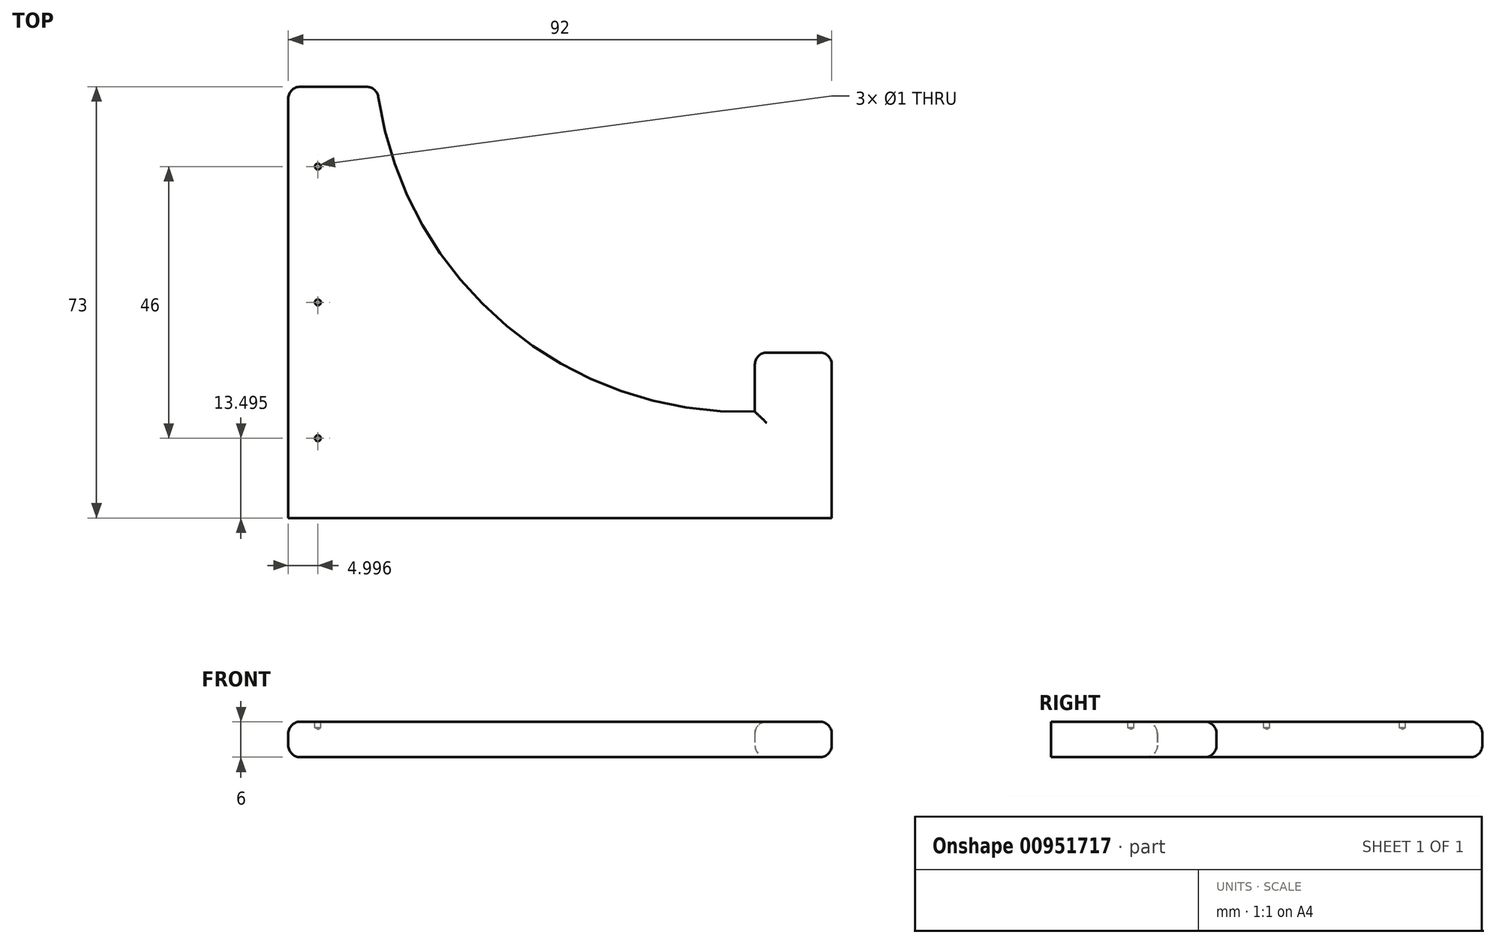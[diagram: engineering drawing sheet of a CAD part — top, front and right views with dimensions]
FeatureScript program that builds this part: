
annotation { "Feature Type Name" : "Feature", "Feature Type Description" : "" }
export const myFeature = defineFeature(function(context is Context, id is Id, definition is map)
    precondition{}
    {
        {
            var Q0;
            Q0=qCreatedBy(makeId("Top.planeOp"),FACE);
            var sketch = newSketch(context, id + "F0", { "sketchPlane" : qUnion([Q0])});
            skLineSegment(sketch, "E0.bottom", {"start": v(-43.17, -8.37) * mm, "end": v(48.83, -8.37) * mm});
            skLineSegment(sketch, "E0.top", {"start": v(-43.17, 64.63) * mm, "end": v(-28.17, 64.63) * mm});
            skLineSegment(sketch, "E0.left", {"start": v(-43.17, -8.37) * mm, "end": v(-43.17, 64.63) * mm});
            skLineSegment(sketch, "E0.right", {"start": v(48.83, -8.37) * mm, "end": v(48.83, 19.63) * mm});
            skLineSegment(sketch, "E1", {"start": v(35.83, 19.63) * mm, "end": v(48.83, 19.63) * mm});
            skLineSegment(sketch, "E2", {"start": v(35.83, 19.63) * mm, "end": v(35.83, 9.63) * mm});
            skArc(sketch, "E3", {"start": v(-28.17, 64.63) * mm, "mid": v(-6.85, 24.7) * mm, "end": v(35.83, 9.63) * mm});
            skSolve(sketch);
        }
        {
            var Q0;
            Q0=makeQuery(id+"F0.imprint","IMPRINT",FACE,{"disambiguationData":[TD([[makeQuery(id+"F0.imprint","IMPRINT",EDGE,{"derivedFrom":sQuery(id+"F0.wireOp",EDGE,"E0.bottom")}),1.0]])]});
            extrude(context, id + "F1", {"entities" : qUnion([Q0]), "depth" : 6 * mm, "offsetDistance" : 25 * mm});
        }
        {
            var Q0;
            Q0=makeQuery(id+"F1.opExtrude","CAP_FACE",FACE,{"disambiguationData":[OSD([sQuery(id+"F0.wireOp",EDGE,"E0.bottom"),sQuery(id+"F0.wireOp",EDGE,"E0.top"),sQuery(id+"F0.wireOp",EDGE,"E0.left"),sQuery(id+"F0.wireOp",EDGE,"E0.right"),sQuery(id+"F0.wireOp",EDGE,"E1"),sQuery(id+"F0.wireOp",EDGE,"E2"),sQuery(id+"F0.wireOp",EDGE,"E3")])],"isStart":false});
            var sketch = newSketch(context, id + "F2", { "sketchPlane" : qUnion([Q0])});
            skPoint(sketch, "E4", {"position": v(-38.17, 51.13) * mm});
            skPoint(sketch, "E5", {"position": v(-38.17, 28.13) * mm});
            skPoint(sketch, "E6", {"position": v(-38.17, 5.13) * mm});
            skSolve(sketch);
        }
        {
            var Q0;
            Q0=sQuery(id+"F2.wireOp",VERTEX,"E4");
            var Q1;
            Q1=sQuery(id+"F2.wireOp",VERTEX,"E5");
            var Q2;
            Q2=sQuery(id+"F2.wireOp",VERTEX,"E6");
            var Q3;
            Q3=makeQuery(id+"F1.opExtrude","SWEPT_BODY",BODY,{"disambiguationData":[OSD([sQuery(id+"F0.wireOp",EDGE,"E0.bottom"),sQuery(id+"F0.wireOp",EDGE,"E0.top"),sQuery(id+"F0.wireOp",EDGE,"E0.left"),sQuery(id+"F0.wireOp",EDGE,"E0.right"),sQuery(id+"F0.wireOp",EDGE,"E1"),sQuery(id+"F0.wireOp",EDGE,"E2"),sQuery(id+"F0.wireOp",EDGE,"E3")])]});
            hole(context, id + "F3", {"style" : HoleStyle.SIMPLE, "endStyle" : HoleEndStyle.BLIND, "holeDiameter" : 1 * mm, "majorDiameter" : 5 * mm, "holeDepth" : 1 * mm, "isTappedThrough" : true, "tappedDepth" : 12 * mm, "tapClearance" : 3, "locations" : qUnion([Q0, Q1, Q2]), "scope" : qUnion([Q3])});
        }
        {
            var Q0;
            Q0=makeQuery(id+"F1.opExtrude","SWEPT_EDGE",EDGE,{"disambiguationData":[OSD([sQuery(id+"F0.wireOp",EDGE,"E0.right"),sQuery(id+"F0.wireOp",EDGE,"E1")])]});
            var Q1;
            Q1=makeQuery(id+"F1.opExtrude","CAP_EDGE",EDGE,{"disambiguationData":[OSD([sQuery(id+"F0.wireOp",EDGE,"E0.right")])],"isStart":true});
            var Q2;
            Q2=makeQuery(id+"F1.opExtrude","CAP_EDGE",EDGE,{"disambiguationData":[OSD([sQuery(id+"F0.wireOp",EDGE,"E0.right")])],"isStart":false});
            var Q3;
            Q3=makeQuery(id+"F1.opExtrude","CAP_EDGE",EDGE,{"disambiguationData":[OSD([sQuery(id+"F0.wireOp",EDGE,"E1")])],"isStart":false});
            var Q4;
            Q4=makeQuery(id+"F1.opExtrude","CAP_EDGE",EDGE,{"disambiguationData":[OSD([sQuery(id+"F0.wireOp",EDGE,"E1")])],"isStart":true});
            var Q5;
            Q5=makeQuery(id+"F1.opExtrude","CAP_EDGE",EDGE,{"disambiguationData":[OSD([sQuery(id+"F0.wireOp",EDGE,"E2")])],"isStart":false});
            var Q6;
            Q6=makeQuery(id+"F1.opExtrude","CAP_EDGE",EDGE,{"disambiguationData":[OSD([sQuery(id+"F0.wireOp",EDGE,"E3")])],"isStart":false});
            var Q7;
            Q7=makeQuery(id+"F1.opExtrude","CAP_EDGE",EDGE,{"disambiguationData":[OSD([sQuery(id+"F0.wireOp",EDGE,"E2")])],"isStart":true});
            var Q8;
            Q8=makeQuery(id+"F1.opExtrude","CAP_EDGE",EDGE,{"disambiguationData":[OSD([sQuery(id+"F0.wireOp",EDGE,"E3")])],"isStart":true});
            var Q9;
            Q9=makeQuery(id+"F1.opExtrude","CAP_EDGE",EDGE,{"disambiguationData":[OSD([sQuery(id+"F0.wireOp",EDGE,"E0.top")])],"isStart":true});
            var Q10;
            Q10=makeQuery(id+"F1.opExtrude","CAP_EDGE",EDGE,{"disambiguationData":[OSD([sQuery(id+"F0.wireOp",EDGE,"E0.top")])],"isStart":false});
            var Q11;
            Q11=makeQuery(id+"F1.opExtrude","CAP_EDGE",EDGE,{"disambiguationData":[OSD([sQuery(id+"F0.wireOp",EDGE,"E0.left")])],"isStart":true});
            var Q12;
            Q12=makeQuery(id+"F1.opExtrude","CAP_EDGE",EDGE,{"disambiguationData":[OSD([sQuery(id+"F0.wireOp",EDGE,"E0.left")])],"isStart":false});
            var Q13;
            Q13=makeQuery(id+"F1.opExtrude","SWEPT_EDGE",EDGE,{"disambiguationData":[OSD([sQuery(id+"F0.wireOp",EDGE,"E1"),sQuery(id+"F0.wireOp",EDGE,"E2")])]});
            var Q14;
            Q14=makeQuery(id+"F1.opExtrude","SWEPT_EDGE",EDGE,{"disambiguationData":[OSD([sQuery(id+"F0.wireOp",EDGE,"E0.top"),sQuery(id+"F0.wireOp",EDGE,"E3")])]});
            var Q15;
            Q15=makeQuery(id+"F1.opExtrude","SWEPT_EDGE",EDGE,{"disambiguationData":[OSD([sQuery(id+"F0.wireOp",EDGE,"E0.top"),sQuery(id+"F0.wireOp",EDGE,"E0.left")])]});
            fillet(context, id + "F4", {"entities" : qUnion([Q0, Q1, Q2, Q3, Q4, Q5, Q6, Q7, Q8, Q9, Q10, Q11, Q12, Q13, Q14, Q15]), "radius" : 2 * mm, "tangentPropagation" : true, "allowEdgeOverflow" : false});
        }
    });
